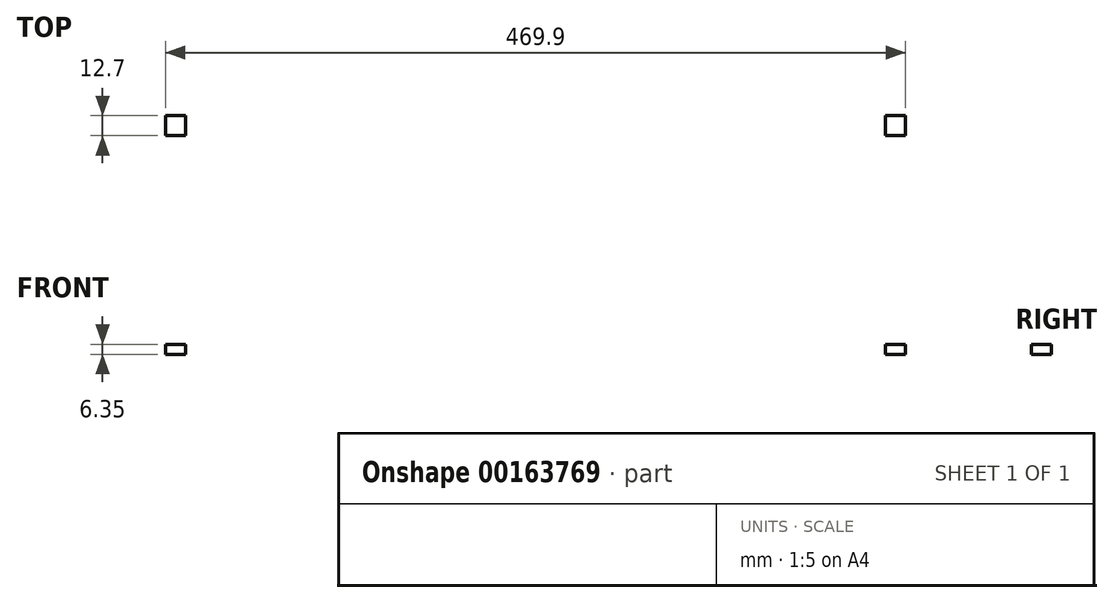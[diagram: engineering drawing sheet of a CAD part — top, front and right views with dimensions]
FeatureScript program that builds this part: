
annotation { "Feature Type Name" : "Feature", "Feature Type Description" : "" }
export const myFeature = defineFeature(function(context is Context, id is Id, definition is map)
    precondition{}
    {
        {
            var Q0;
            Q0=qCreatedBy(makeId("Top.planeOp"),FACE);
            var sketch = newSketch(context, id + "F0", { "sketchPlane" : qUnion([Q0])});
            skLineSegment(sketch, "E0.bottom", {"start": v(234.95, 234.95) * mm, "end": v(-234.95, 234.95) * mm});
            skLineSegment(sketch, "E0.top", {"start": v(234.95, -234.95) * mm, "end": v(-234.95, -234.95) * mm});
            skLineSegment(sketch, "E0.left", {"start": v(234.95, 234.95) * mm, "end": v(234.95, -234.95) * mm});
            skLineSegment(sketch, "E0.right", {"start": v(-234.95, 234.95) * mm, "end": v(-234.95, -234.95) * mm});
            skPoint(sketch, "E0.middle", {"position": v(0, 0) * mm});
            skLineSegment(sketch, "E1.bottom", {"start": v(-234.95, 234.95) * mm, "end": v(-222.25, 234.95) * mm});
            skLineSegment(sketch, "E1.top", {"start": v(-234.95, 222.25) * mm, "end": v(-222.25, 222.25) * mm});
            skLineSegment(sketch, "E1.left", {"start": v(-234.95, 234.95) * mm, "end": v(-234.95, 222.25) * mm});
            skLineSegment(sketch, "E1.right", {"start": v(-222.25, 234.95) * mm, "end": v(-222.25, 222.25) * mm});
            skLineSegment(sketch, "E2.bottom", {"start": v(234.95, 234.95) * mm, "end": v(222.25, 234.95) * mm});
            skLineSegment(sketch, "E2.top", {"start": v(234.95, 222.25) * mm, "end": v(222.25, 222.25) * mm});
            skLineSegment(sketch, "E2.left", {"start": v(234.95, 234.95) * mm, "end": v(234.95, 222.25) * mm});
            skLineSegment(sketch, "E2.right", {"start": v(222.25, 234.95) * mm, "end": v(222.25, 222.25) * mm});
            skLineSegment(sketch, "E3.bottom", {"start": v(234.95, -234.95) * mm, "end": v(222.25, -234.95) * mm});
            skLineSegment(sketch, "E3.top", {"start": v(234.95, -222.25) * mm, "end": v(222.25, -222.25) * mm});
            skLineSegment(sketch, "E3.left", {"start": v(234.95, -234.95) * mm, "end": v(234.95, -222.25) * mm});
            skLineSegment(sketch, "E3.right", {"start": v(222.25, -234.95) * mm, "end": v(222.25, -222.25) * mm});
            skLineSegment(sketch, "E4.bottom", {"start": v(-234.95, -234.95) * mm, "end": v(-222.25, -234.95) * mm});
            skLineSegment(sketch, "E4.top", {"start": v(-234.95, -222.25) * mm, "end": v(-222.25, -222.25) * mm});
            skLineSegment(sketch, "E4.left", {"start": v(-234.95, -234.95) * mm, "end": v(-234.95, -222.25) * mm});
            skLineSegment(sketch, "E4.right", {"start": v(-222.25, -234.95) * mm, "end": v(-222.25, -222.25) * mm});
            skSolve(sketch);
        }
        {
            var Q0;
            Q0=makeQuery(id+"F0.imprint","IMPRINT",FACE,{"disambiguationData":[TD([[makeQuery(id+"F0.imprint","IMPRINT",EDGE,{"derivedFrom":sQuery(id+"F0.wireOp",EDGE,"E0.bottom")}),1.0]])]});
            extrude(context, id + "F1", {"entities" : qUnion([Q0]), "depth" : 6.35 * mm});
        }
    });
